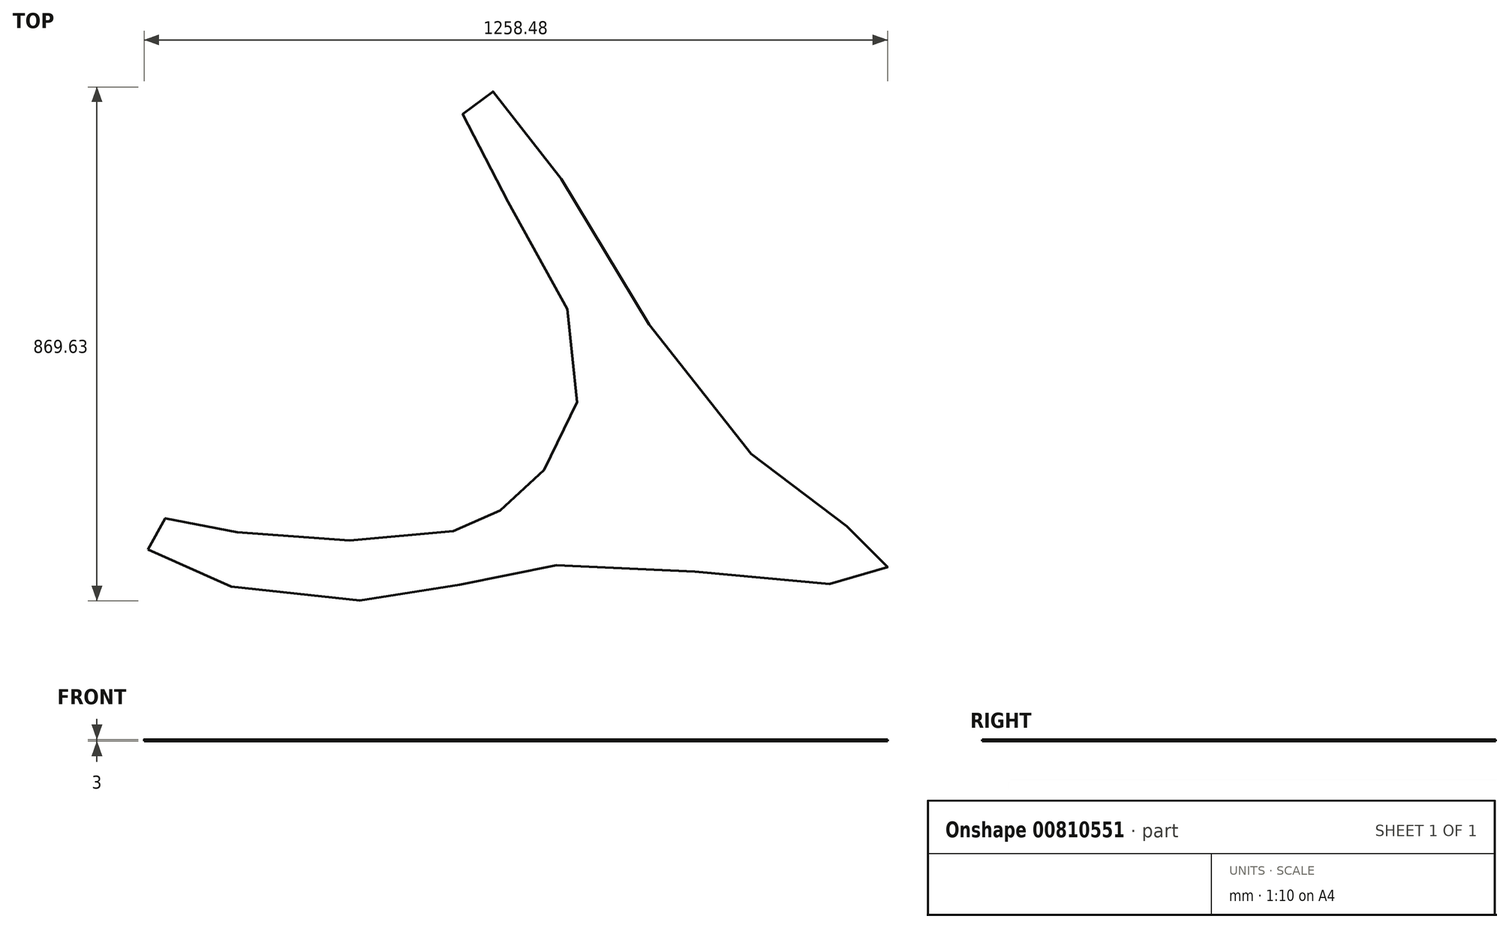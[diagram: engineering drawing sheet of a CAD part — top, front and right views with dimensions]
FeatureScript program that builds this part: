
annotation { "Feature Type Name" : "Feature", "Feature Type Description" : "" }
export const myFeature = defineFeature(function(context is Context, id is Id, definition is map)
    precondition{}
    {
        {
            var Q0;
            Q0=qCreatedBy(makeId("Top.planeOp"),FACE);
            var sketch = newSketch(context, id + "F0", { "sketchPlane" : qUnion([Q0])});
            skFitSpline(sketch, "E0", {"points": [v(-815.57, 150) * mm, v(-429.27, 64.58) * mm, v(-107.02, 124.76) * mm, v(414.18, 98.3) * mm, v(433.4, 133.98) * mm, v(164.36, 353.6) * mm, v(-239, 929.73) * mm, v(-283.85, 901.4) * mm, v(-108.87, 565.09) * mm, v(-118.63, 320.75) * mm, v(-213.04, 221.62) * mm, v(-275.91, 186.88) * mm, v(-640.86, 175.23) * mm, v(-803.92, 198.53) * mm, v(-815.57, 150) * mm]});
            skSolve(sketch);
        }
        {
            var Q0;
            Q0 = qSketchRegion(id + "F0", true);
            extrude(context, id + "F1", {"entities" : qUnion([Q0]), "endBound" : BoundingType.SYMMETRIC, "depth" : 3 * mm, "offsetDistance" : 25 * mm});
        }
        {
            var Q0;
            Q0=makeQuery(id+"F1.opExtrude","CAP_FACE",FACE,{"disambiguationData":[OSD([sQuery(id+"F0.wireOp",EDGE,"E0")])],"isStart":false});
            var sketch = newSketch(context, id + "F2", { "sketchPlane" : qUnion([Q0])});
            skPoint(sketch, "E1", {"position": v(0, 255.94) * mm});
            skSolve(sketch);
        }
    });
